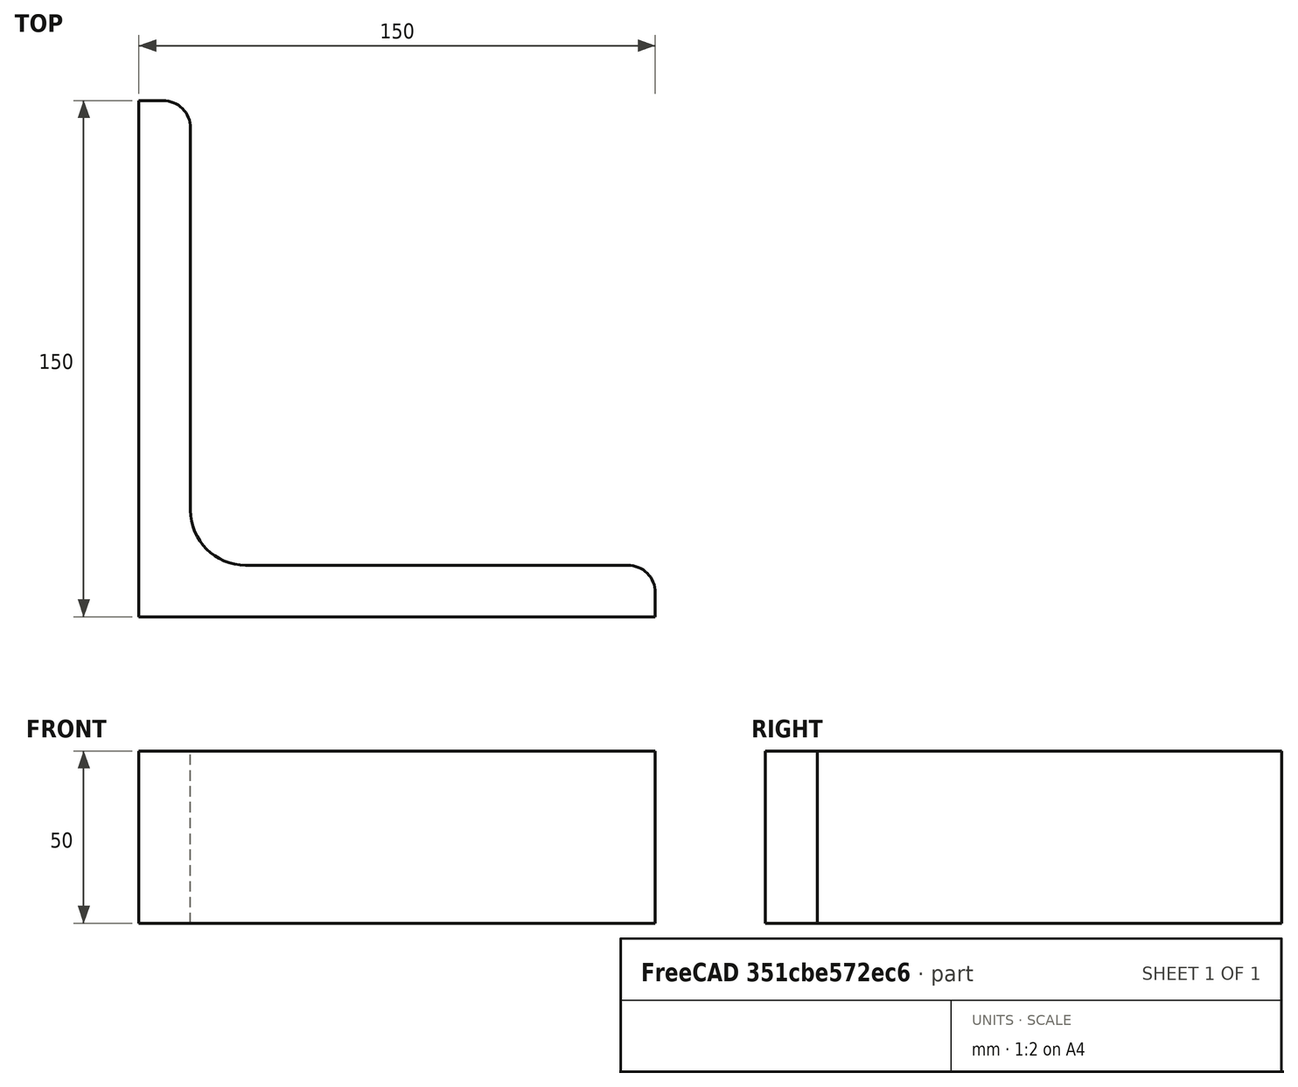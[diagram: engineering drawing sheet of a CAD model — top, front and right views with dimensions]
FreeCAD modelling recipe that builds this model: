
FCSTD DOCUMENT  (FreeCAD 0.15R4671 (Git))
Label: Angle Bar L150x150x15 EN10056 S235JR
License: All rights reserved
LicenseURL: http://en.wikipedia.org/wiki/All_rights_reserved
objects: Sketcher::SketchObject×1, Part::Extrusion×1
note: 2 computed .brp shape members not serialized (recipe doc carries the construction recipe); baked Part::Feature solids carry a one-line shape summary decoded from their .brp

FEATURE [Sketcher::SketchObject] Sketch
  sketch-geometry (9):
    g0: LineSegment StartX=0 StartY=0 StartZ=0 EndX=150 EndY=0 EndZ=0
    g1: LineSegment StartX=150 StartY=0 StartZ=0 EndX=150 EndY=7 EndZ=0
    g2: LineSegment StartX=142 StartY=15 StartZ=0 EndX=31 EndY=15 EndZ=0
    g3: LineSegment StartX=0 StartY=0 StartZ=0 EndX=0 EndY=150 EndZ=0
    g4: LineSegment StartX=0 StartY=150 StartZ=0 EndX=7 EndY=150 EndZ=0
    g5: LineSegment StartX=15 StartY=142 StartZ=0 EndX=15 EndY=31 EndZ=0
    g6: ArcOfCircle CenterX=31 CenterY=31 CenterZ=0 NormalX=0 NormalY=0 NormalZ=1 Radius=16 StartAngle=3.14159 EndAngle=4.71239
    g7: ArcOfCircle CenterX=7 CenterY=142 CenterZ=0 NormalX=0 NormalY=0 NormalZ=1 Radius=8 StartAngle=0 EndAngle=1.5708
    g8: ArcOfCircle CenterX=142 CenterY=7 CenterZ=0 NormalX=0 NormalY=0 NormalZ=1 Radius=8 StartAngle=0 EndAngle=1.5708
  constraints (23):
    c: Coincident(g0,g-1)
    c: Horizontal(g0)
    c: Coincident(g1,g0)
    c: Vertical(g1)
    c: Horizontal(g2)
    c: Coincident(g3,g-1)
    c: Vertical(g3)
    c: Coincident(g4,g3)
    c: Horizontal(g4)
    c: Vertical(g5)
    c: Tangent(g5,g6) = -1.5708
    c: Tangent(g2,g6) = 1.5708
    c: Tangent(g4,g7) = 1.5708
    c: Tangent(g5,g7) = 1.5708
    c: Tangent(g2,g8) = -1.5708
    c: Tangent(g1,g8) = -1.5708
    c: DistanceX(g0) = 150
    c: DistanceY(g3) = 150
    c: DistanceY(g0,g2) = 15
    c: DistanceX(g3,g5) = 15
    c: Radius(g6) = 16
    c: Radius(g8) = 8
    c: Radius(g7) = 8
FEATURE [Part::Extrusion] Extrude  label="Angle Bar L150x150x15 EN10056 S235JR"
  Base = -> Sketch
  Dir = (0,0,50)
  Solid = true
